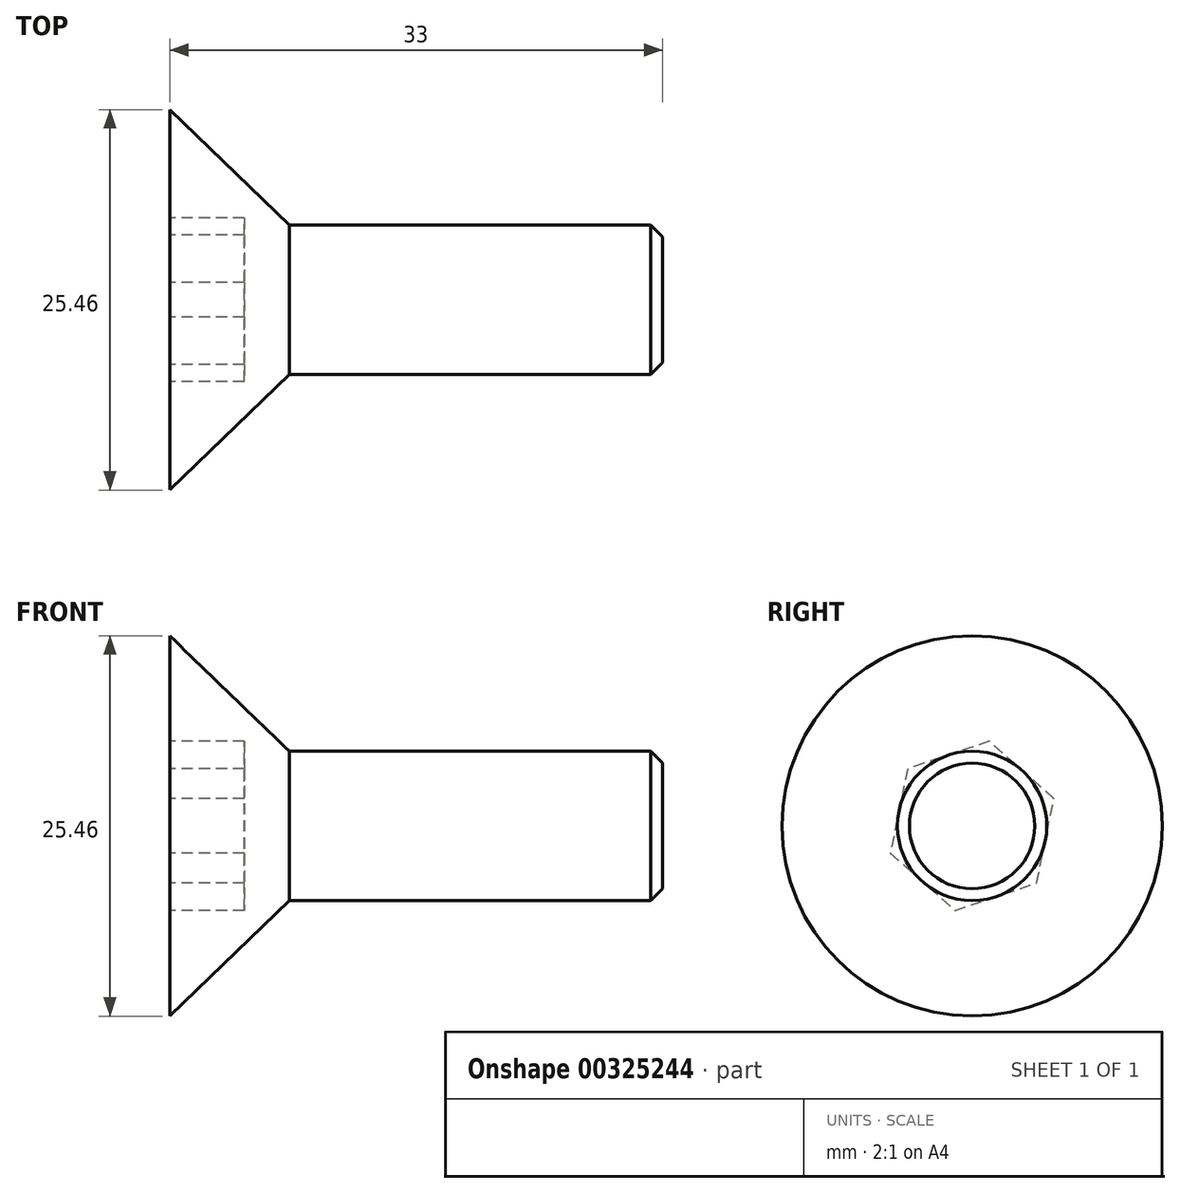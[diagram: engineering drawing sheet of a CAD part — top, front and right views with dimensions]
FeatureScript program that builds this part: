
annotation { "Feature Type Name" : "Feature", "Feature Type Description" : "" }
export const myFeature = defineFeature(function(context is Context, id is Id, definition is map)
    precondition{}
    {
        {
            var Q0;
            Q0=qCreatedBy(makeId("Front.planeOp"),FACE);
            var sketch = newSketch(context, id + "F0", { "sketchPlane" : qUnion([Q0])});
            skLineSegment(sketch, "E0", {"start": v(0, 0) * mm, "end": v(0, 12.73) * mm});
            skLineSegment(sketch, "E1", {"start": v(0, 12.73) * mm, "end": v(8, 5) * mm});
            skLineSegment(sketch, "E2", {"start": v(8, 5) * mm, "end": v(33, 5) * mm});
            skLineSegment(sketch, "E3", {"start": v(33, 5) * mm, "end": v(33, 0) * mm});
            skLineSegment(sketch, "E4", {"start": v(33, 0) * mm, "end": v(45.83, 0) * mm, "construction": true});
            skLineSegment(sketch, "E5", {"start": v(0, 0) * mm, "end": v(33, 0) * mm});
            skSolve(sketch);
        }
        {
            var Q0;
            Q0=makeQuery(id+"F0.imprint","IMPRINT",FACE,{"disambiguationData":[TD([[makeQuery(id+"F0.imprint","IMPRINT",EDGE,{"derivedFrom":sQuery(id+"F0.wireOp",EDGE,"E0")}),-1.0]])]});
            var Q1;
            Q1=sQuery(id+"F0.wireOp",EDGE,"E5");
            revolve(context, id + "F1", {"entities" : qUnion([Q0]), "axis" : qUnion([Q1]), "revolveType" : RevolveType.FULL});
        }
        {
            var Q0;
            Q0=makeQuery(id+"F1.opRevolve","SWEPT_FACE",FACE,{"disambiguationData":[OSD([sQuery(id+"F0.wireOp",EDGE,"E0")])]});
            var sketch = newSketch(context, id + "F2", { "sketchPlane" : qUnion([Q0])});
            skCircle(sketch, "E6.cCircle", {"center": v(0, 0) * mm, "radius": 5 * mm, "construction": true});
            skLineSegment(sketch, "E6.0", {"start": v(1.15, -5.66) * mm, "end": v(-4.32, -3.83) * mm});
            skLineSegment(sketch, "E6.1", {"start": v(-4.32, -3.83) * mm, "end": v(-5.48, 1.83) * mm});
            skLineSegment(sketch, "E6.2", {"start": v(-5.48, 1.83) * mm, "end": v(-1.15, 5.66) * mm});
            skLineSegment(sketch, "E6.3", {"start": v(-1.15, 5.66) * mm, "end": v(4.32, 3.83) * mm});
            skLineSegment(sketch, "E6.4", {"start": v(4.32, 3.83) * mm, "end": v(5.48, -1.83) * mm});
            skLineSegment(sketch, "E6.5", {"start": v(5.48, -1.83) * mm, "end": v(1.15, -5.66) * mm});
            skPoint(sketch, "E6.0.midPoint", {"position": v(-1.59, -4.74) * mm});
            skSolve(sketch);
        }
        {
            var Q0;
            Q0=makeQuery(id+"F2.imprint","IMPRINT",FACE,{"disambiguationData":[TD([[makeQuery(id+"F2.imprint","IMPRINT",EDGE,{"derivedFrom":sQuery(id+"F2.wireOp",EDGE,"E6.0")}),-1.0]])]});
            extrude(context, id + "F3", {"entities" : qUnion([Q0]), "operationType" : NewBodyOperationType.REMOVE, "oppositeDirection" : true, "depth" : 5 * mm});
        }
        {
            var Q0;
            Q0=makeQuery(id+"F1.opRevolve","SWEPT_EDGE",EDGE,{"disambiguationData":[OSD([sQuery(id+"F0.wireOp",EDGE,"E2"),sQuery(id+"F0.wireOp",EDGE,"E3")])]});
            chamfer(context, id + "F4", {"entities" : qUnion([Q0]), "width" : 0.8 * mm, "tangentPropagation" : true});
        }
    });
